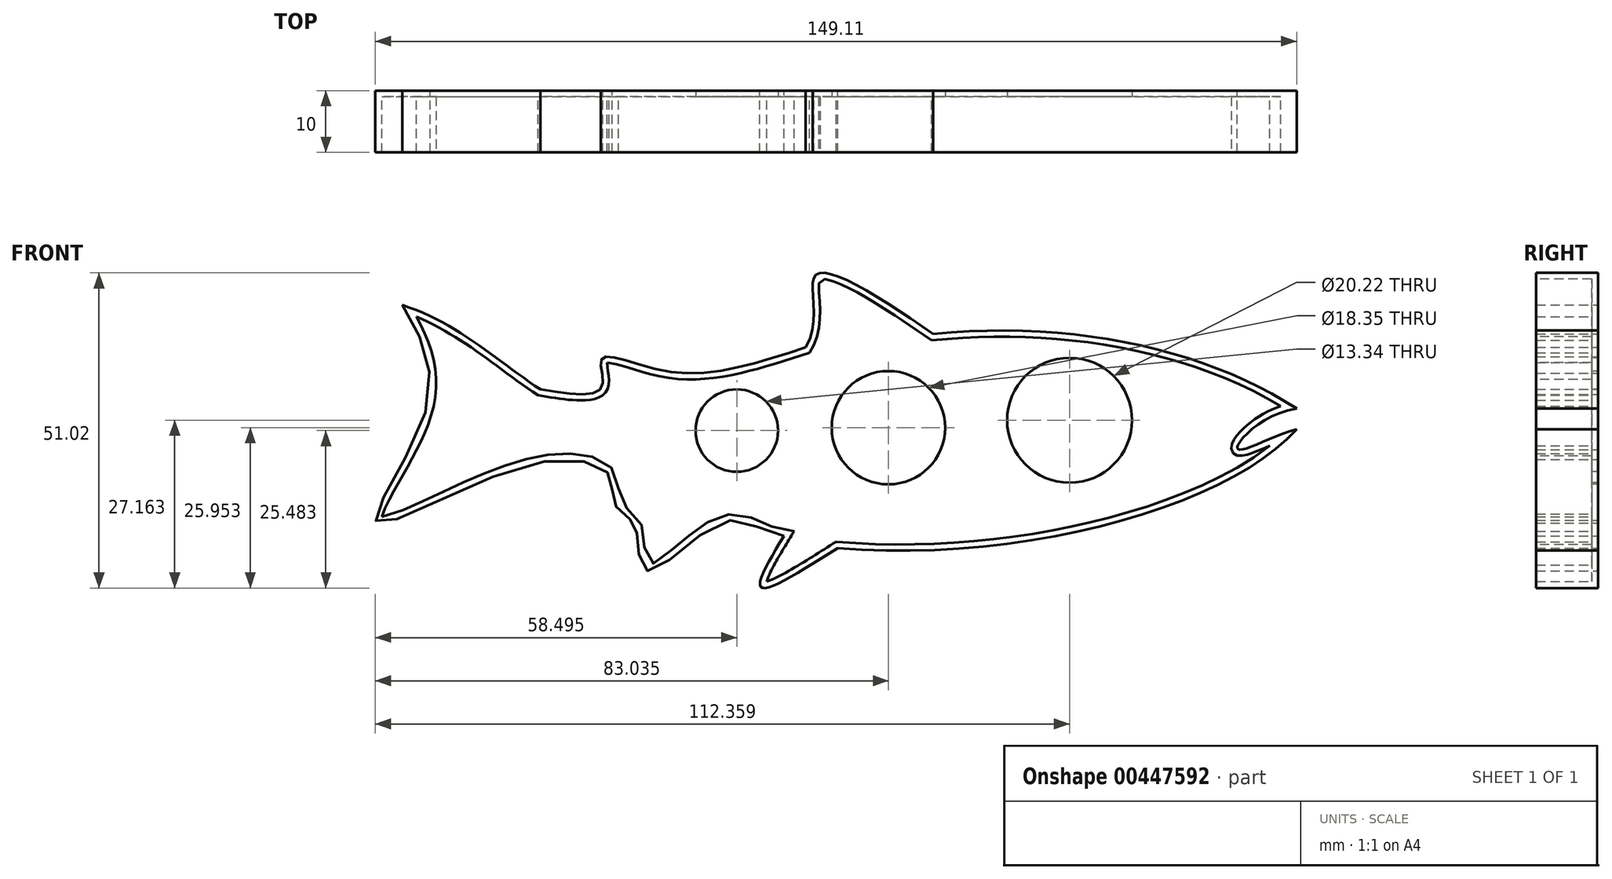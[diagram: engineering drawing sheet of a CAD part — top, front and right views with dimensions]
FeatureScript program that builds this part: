
annotation { "Feature Type Name" : "Feature", "Feature Type Description" : "" }
export const myFeature = defineFeature(function(context is Context, id is Id, definition is map)
    precondition{}
    {
        {
            var Q0;
            Q0=qCreatedBy(makeId("Front.planeOp"),FACE);
            var sketch = newSketch(context, id + "F0", { "sketchPlane" : qUnion([Q0])});
            skFitSpline(sketch, "E0", {"points": [v(-70.45, 35.06) * mm, v(-48.14, 21.4) * mm], "startDerivative": vector(26.42, -8.37) * mm, "endDerivative": vector(21.14, -14.1) * mm});
            skFitSpline(sketch, "E1", {"points": [v(-70.45, 35.06) * mm, v(-66.59, 18.06) * mm, v(-74.64, 0) * mm, v(-49.63, 9.32) * mm, v(-36.78, 7.27) * mm, v(-36.27, 3.15) * mm, v(-33.19, 0) * mm, v(-32.33, -3.53) * mm, v(-30.62, -7.98) * mm, v(-18.45, 0) * mm, v(-8.69, -2.33) * mm], "startDerivative": vector(68.08, -114.17) * mm, "endDerivative": vector(112.29, -16.04) * mm});
            skFitSpline(sketch, "E2", {"points": [v(-8.69, -2.33) * mm, v(-12.42, -10.59) * mm, v(0, -4.26) * mm], "startDerivative": vector(-15.23, -25.19) * mm, "endDerivative": vector(30.96, 19.71) * mm});
            skPoint(sketch, "E3.1.internal.snap0", {"position": v(75.58, 14.97) * mm});
            skFitSpline(sketch, "E3", {"points": [v(0, -4.26) * mm, v(74.3, 14.97) * mm], "startDerivative": vector(89.27, -7.72) * mm, "endDerivative": vector(33.4, 37.74) * mm});
            skFitSpline(sketch, "E4", {"points": [v(74.3, 14.97) * mm, v(64.75, 11.78) * mm, v(74.3, 18.3) * mm], "startDerivative": vector(-24.57, -6.96) * mm, "endDerivative": vector(33.2, 4.61) * mm});
            skFitSpline(sketch, "E5", {"points": [v(74.3, 18.3) * mm, v(15.44, 30.39) * mm], "startDerivative": vector(-44.86, 29.1) * mm, "endDerivative": vector(-67.76, -6.68) * mm});
            skFitSpline(sketch, "E6", {"points": [v(15.44, 30.39) * mm, v(-3.6, 39.9) * mm, v(-5.2, 28.2) * mm], "startDerivative": vector(-41.64, 29.18) * mm, "endDerivative": vector(-19.33, -30.6) * mm});
            skFitSpline(sketch, "E7", {"points": [v(-5.2, 28.2) * mm, v(-27.42, 24.31) * mm, v(-38.19, 26.37) * mm, v(-38.19, 21.8) * mm, v(-48.14, 21.4) * mm], "startDerivative": vector(-64.32, -20.7) * mm, "endDerivative": vector(-54.2, 8.9) * mm});
            skSolve(sketch);
        }
        {
            var Q0;
            Q0 = qSketchRegion(id + "F0", true);
            var Q1;
            Q1=makeQuery(id+"F0.imprint","IMPRINT",FACE,{"disambiguationData":[TD([[makeQuery(id+"F0.imprint","IMPRINT",EDGE,{"derivedFrom":sQuery(id+"F0.wireOp",EDGE,"E0")}),-1.0]])]});
            extrude(context, id + "F1", {"entities" : qUnion([Q0, Q1]), "depth" : 10 * mm});
        }
        {
            var Q0;
            Q0=makeQuery(id+"F1.opExtrude","CAP_FACE",FACE,{"disambiguationData":[OSD([sQuery(id+"F0.wireOp",EDGE,"E0"),sQuery(id+"F0.wireOp",EDGE,"E1"),sQuery(id+"F0.wireOp",EDGE,"E2"),sQuery(id+"F0.wireOp",EDGE,"E3"),sQuery(id+"F0.wireOp",EDGE,"E4"),sQuery(id+"F0.wireOp",EDGE,"E5"),sQuery(id+"F0.wireOp",EDGE,"E6"),sQuery(id+"F0.wireOp",EDGE,"E7")])],"isStart":false});
            shell(context, id + "F2", {"entities" : qUnion([Q0]), "thickness" : 1 * mm});
        }
        {
            var Q0;
            Q0=makeQuery(id+"F2.opShell","OFFSET_FACE",FACE,{"disambiguationData":[OSD([sQuery(id+"F0.wireOp",EDGE,"E0"),sQuery(id+"F0.wireOp",EDGE,"E1"),sQuery(id+"F0.wireOp",EDGE,"E2"),sQuery(id+"F0.wireOp",EDGE,"E3"),sQuery(id+"F0.wireOp",EDGE,"E4"),sQuery(id+"F0.wireOp",EDGE,"E5"),sQuery(id+"F0.wireOp",EDGE,"E6"),sQuery(id+"F0.wireOp",EDGE,"E7")])]});
            var sketch = newSketch(context, id + "F3", { "sketchPlane" : qUnion([Q0])});
            skCircle(sketch, "E8", {"center": v(-16.33, 14.74) * mm, "radius": 6.67 * mm});
            skCircle(sketch, "E9", {"center": v(8.21, 15.21) * mm, "radius": 9.17 * mm});
            skCircle(sketch, "E10", {"center": v(37.54, 16.42) * mm, "radius": 10.1 * mm});
            skSolve(sketch);
        }
        {
            var Q0;
            Q0=makeQuery(id+"F3.imprint","IMPRINT",FACE,{"disambiguationData":[TD([[makeQuery(id+"F3.imprint","IMPRINT",EDGE,{"derivedFrom":sQuery(id+"F3.wireOp",EDGE,"E8")}),1.0]])]});
            var Q1;
            Q1=makeQuery(id+"F3.imprint","IMPRINT",FACE,{"disambiguationData":[TD([[makeQuery(id+"F3.imprint","IMPRINT",EDGE,{"derivedFrom":sQuery(id+"F3.wireOp",EDGE,"E9")}),1.0]])]});
            var Q2;
            Q2=makeQuery(id+"F3.imprint","IMPRINT",FACE,{"disambiguationData":[TD([[makeQuery(id+"F3.imprint","IMPRINT",EDGE,{"derivedFrom":sQuery(id+"F3.wireOp",EDGE,"E10")}),1.0]])]});
            extrude(context, id + "F4", {"entities" : qUnion([Q0, Q1, Q2]), "operationType" : NewBodyOperationType.REMOVE, "oppositeDirection" : true, "depth" : 25 * mm});
        }
    });
